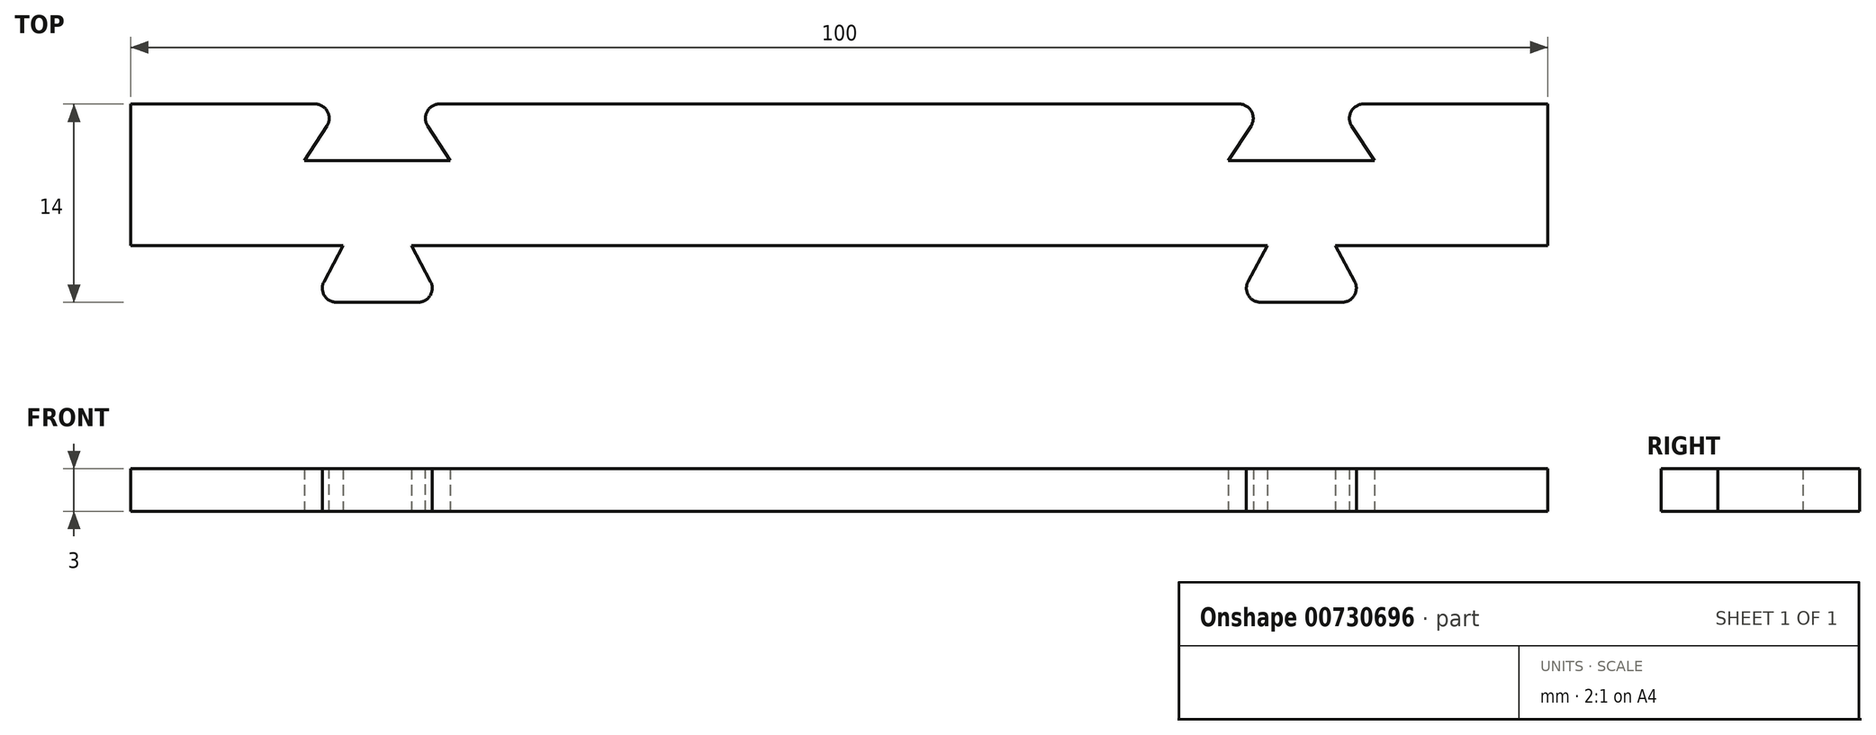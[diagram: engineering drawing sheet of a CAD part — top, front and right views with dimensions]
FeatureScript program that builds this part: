
annotation { "Feature Type Name" : "Feature", "Feature Type Description" : "" }
export const myFeature = defineFeature(function(context is Context, id is Id, definition is map)
    precondition{}
    {
        {
            var Q0;
            Q0=qCreatedBy(makeId("Top.planeOp"),FACE);
            var sketch = newSketch(context, id + "F0", { "sketchPlane" : qUnion([Q0])});
            skLineSegment(sketch, "E0.bottom", {"start": v(50, -5) * mm, "end": v(-50, -5) * mm});
            skLineSegment(sketch, "E0.top", {"start": v(50, 5) * mm, "end": v(-50, 5) * mm});
            skLineSegment(sketch, "E0.left", {"start": v(50, -5) * mm, "end": v(50, 5) * mm});
            skLineSegment(sketch, "E0.right", {"start": v(-50, -5) * mm, "end": v(-50, 5) * mm});
            skPoint(sketch, "E0.middle", {"position": v(0, 0) * mm});
            skLineSegment(sketch, "E1", {"start": v(-50, -5) * mm, "end": v(-35, -5) * mm, "construction": true});
            skLineSegment(sketch, "E2", {"start": v(50, -5) * mm, "end": v(35, -5) * mm, "construction": true});
            skLineSegment(sketch, "E3", {"start": v(-50, 5) * mm, "end": v(-35.15, 5) * mm, "construction": true});
            skLineSegment(sketch, "E4", {"start": v(50, 5) * mm, "end": v(35.15, 5) * mm, "construction": true});
            skLineSegment(sketch, "E5", {"start": v(-35, -5) * mm, "end": v(-30.2, -5) * mm, "construction": true});
            skLineSegment(sketch, "E6", {"start": v(-35, -5) * mm, "end": v(-37.15, -9) * mm});
            skLineSegment(sketch, "E7", {"start": v(-37.15, -9) * mm, "end": v(-28.05, -9) * mm});
            skLineSegment(sketch, "E8", {"start": v(-28.05, -9) * mm, "end": v(-30.2, -5) * mm});
            skLineSegment(sketch, "E9", {"start": v(-32.6, -9) * mm, "end": v(-32.6, -5) * mm, "construction": true});
            skLineSegment(sketch, "E10", {"start": v(-35.15, 5) * mm, "end": v(-30.05, 5) * mm, "construction": true});
            skLineSegment(sketch, "E11", {"start": v(-35.15, 5) * mm, "end": v(-37.75, 1) * mm});
            skLineSegment(sketch, "E12", {"start": v(-37.75, 1) * mm, "end": v(-27.45, 1) * mm});
            skLineSegment(sketch, "E13", {"start": v(-27.45, 1) * mm, "end": v(-30.05, 5) * mm});
            skPoint(sketch, "E14.endSnap0", {"position": v(-32.6, 1) * mm});
            skLineSegment(sketch, "E15", {"start": v(-32.6, 1) * mm, "end": v(-32.6, 5) * mm, "construction": true});
            skLineSegment(sketch, "E16", {"start": v(35.15, 5) * mm, "end": v(30.05, 5) * mm, "construction": true});
            skLineSegment(sketch, "E17", {"start": v(35, -5) * mm, "end": v(30.2, -5) * mm, "construction": true});
            skLineSegment(sketch, "E18", {"start": v(35.15, 5) * mm, "end": v(37.75, 1) * mm});
            skLineSegment(sketch, "E19", {"start": v(37.75, 1) * mm, "end": v(27.45, 1) * mm});
            skLineSegment(sketch, "E20", {"start": v(27.45, 1) * mm, "end": v(30.05, 5) * mm});
            skLineSegment(sketch, "E21", {"start": v(35, -5) * mm, "end": v(37.15, -9) * mm});
            skLineSegment(sketch, "E22", {"start": v(37.15, -9) * mm, "end": v(28.05, -9) * mm});
            skLineSegment(sketch, "E23", {"start": v(28.05, -9) * mm, "end": v(30.2, -5) * mm});
            skLineSegment(sketch, "E24", {"start": v(32.6, 1) * mm, "end": v(32.6, 5) * mm, "construction": true});
            skLineSegment(sketch, "E25", {"start": v(32.6, -9) * mm, "end": v(32.6, -5) * mm, "construction": true});
            skSolve(sketch);
        }
        {
            var Q0;
            {var subQ0=sQuery(id+"F0.wireOp",EDGE,"E0.left");Q0=makeQuery(id+"F0.imprint","IMPRINT",FACE,{"disambiguationData":[TD([[makeQuery(id+"F0.imprint","IMPRINT",EDGE,{"derivedFrom":subQ0}),1.0]])]});}
            var Q1;
            {var subQ0=sQuery(id+"F0.wireOp",EDGE,"E6");Q1=makeQuery(id+"F0.imprint","IMPRINT",FACE,{"disambiguationData":[TD([[makeQuery(id+"F0.imprint","IMPRINT",EDGE,{"derivedFrom":subQ0}),1.0]])]});}
            var Q2;
            {var subQ0=sQuery(id+"F0.wireOp",EDGE,"E21");Q2=makeQuery(id+"F0.imprint","IMPRINT",FACE,{"disambiguationData":[TD([[makeQuery(id+"F0.imprint","IMPRINT",EDGE,{"derivedFrom":subQ0}),-1.0]])]});}
            extrude(context, id + "F1", {"entities" : qUnion([Q0, Q1, Q2]), "depth" : 3 * mm, "offsetDistance" : 25 * mm});
        }
        {
            var Q0;
            Q0=makeQuery(id+"F1.opExtrude","SWEPT_EDGE",EDGE,{"disambiguationData":[OSD([sQuery(id+"F0.wireOp",EDGE,"E7"),sQuery(id+"F0.wireOp",EDGE,"E8")])]});
            var Q1;
            Q1=makeQuery(id+"F1.opExtrude","SWEPT_EDGE",EDGE,{"disambiguationData":[OSD([sQuery(id+"F0.wireOp",EDGE,"E6"),sQuery(id+"F0.wireOp",EDGE,"E7")])]});
            var Q2;
            Q2=makeQuery(id+"F1.opExtrude","SWEPT_EDGE",EDGE,{"disambiguationData":[OSD([sQuery(id+"F0.wireOp",EDGE,"E21"),sQuery(id+"F0.wireOp",EDGE,"E22")])]});
            var Q3;
            Q3=makeQuery(id+"F1.opExtrude","SWEPT_EDGE",EDGE,{"disambiguationData":[OSD([sQuery(id+"F0.wireOp",EDGE,"E22"),sQuery(id+"F0.wireOp",EDGE,"E23")])]});
            var Q4;
            Q4=makeQuery(id+"F1.opExtrude","SWEPT_EDGE",EDGE,{"disambiguationData":[OSD([sQuery(id+"F0.wireOp",EDGE,"E0.top"),sQuery(id+"F0.wireOp",EDGE,"E20")])]});
            var Q5;
            Q5=makeQuery(id+"F1.opExtrude","SWEPT_EDGE",EDGE,{"disambiguationData":[OSD([sQuery(id+"F0.wireOp",EDGE,"E0.top"),sQuery(id+"F0.wireOp",EDGE,"E11")])]});
            var Q6;
            Q6=makeQuery(id+"F1.opExtrude","SWEPT_EDGE",EDGE,{"disambiguationData":[OSD([sQuery(id+"F0.wireOp",EDGE,"E0.top"),sQuery(id+"F0.wireOp",EDGE,"E13")])]});
            var Q7;
            Q7=makeQuery(id+"F1.opExtrude","SWEPT_EDGE",EDGE,{"disambiguationData":[OSD([sQuery(id+"F0.wireOp",EDGE,"E0.top"),sQuery(id+"F0.wireOp",EDGE,"E18")])]});
            fillet(context, id + "F2", {"entities" : qUnion([Q0, Q1, Q2, Q3, Q4, Q5, Q6, Q7]), "radius" : 1 * mm, "tangentPropagation" : true, "allowEdgeOverflow" : false});
        }
    });
